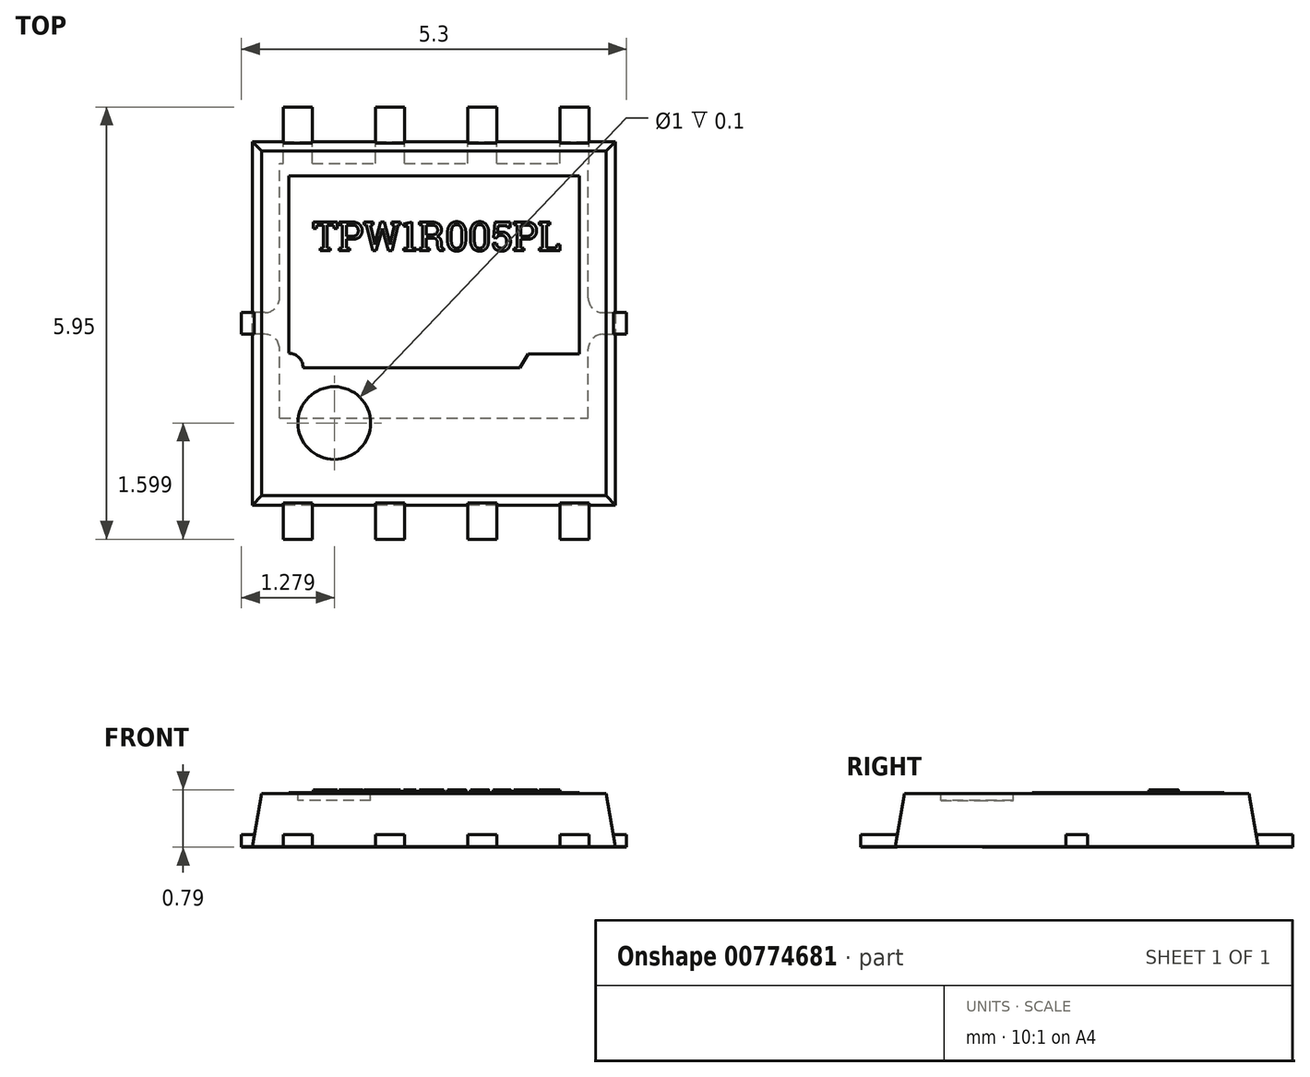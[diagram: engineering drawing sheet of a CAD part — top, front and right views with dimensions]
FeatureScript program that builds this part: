
annotation { "Feature Type Name" : "Feature", "Feature Type Description" : "" }
export const myFeature = defineFeature(function(context is Context, id is Id, definition is map)
    precondition{}
    {
        {
            var Q0;
            Q0=qCreatedBy(makeId("Top.planeOp"),FACE);
            cPlane(context, id + "F0", {"entities" : qUnion([Q0]), "cplaneType" : CPlaneType.OFFSET, "offset" : 0.17 * mm, "width" : 150 * mm, "height" : 150 * mm});
        }
        {
            var Q0;
            Q0=qCreatedBy(makeId("Top.planeOp"),FACE);
            var sketch = newSketch(context, id + "F1", { "sketchPlane" : qUnion([Q0])});
            skLineSegment(sketch, "E0.bottom", {"start": v(2.5, -2.5) * mm, "end": v(-2.5, -2.5) * mm});
            skLineSegment(sketch, "E0.top", {"start": v(2.5, 2.5) * mm, "end": v(-2.5, 2.5) * mm});
            skLineSegment(sketch, "E0.left", {"start": v(2.5, -2.5) * mm, "end": v(2.5, 2.5) * mm});
            skLineSegment(sketch, "E0.right", {"start": v(-2.5, -2.5) * mm, "end": v(-2.5, 2.5) * mm});
            skPoint(sketch, "E0.middle", {"position": v(0, 0) * mm});
            skSolve(sketch);
        }
        {
            var Q0;
            Q0 = qSketchRegion(id + "F1", true);
            extrude(context, id + "F2", {"entities" : qUnion([Q0]), "depth" : 0.73 * mm, "offsetDistance" : 25 * mm, "hasDraft" : true, "draftAngle" : 10 * degree, "draftPullDirection" : true});
        }
        {
            var Q0;
            Q0=qCreatedBy(id+"F0.planeOp",FACE);
            var sketch = newSketch(context, id + "F3", { "sketchPlane" : qUnion([Q0])});
            skLineSegment(sketch, "E1.bottom", {"start": v(-2.08, -2.47) * mm, "end": v(-1.68, -2.47) * mm});
            skLineSegment(sketch, "E1.top", {"start": v(-2.08, -2.97) * mm, "end": v(-1.68, -2.97) * mm});
            skLineSegment(sketch, "E1.left", {"start": v(-2.08, -2.47) * mm, "end": v(-2.08, -2.97) * mm});
            skLineSegment(sketch, "E1.right", {"start": v(-1.68, -2.47) * mm, "end": v(-1.68, -2.97) * mm});
            skLineSegment(sketch, "E2", {"start": v(-2.47, -2.47) * mm, "end": v(2.47, -2.47) * mm, "construction": true});
            skLineSegment(sketch, "E3", {"start": v(2.47, 2.47) * mm, "end": v(-2.47, 2.47) * mm, "construction": true});
            skLineSegment(sketch, "E4", {"start": v(2.47, -2.47) * mm, "end": v(2.47, 2.47) * mm, "construction": true});
            skLineSegment(sketch, "E5", {"start": v(-2.47, 2.47) * mm, "end": v(-2.47, -2.47) * mm, "construction": true});
            skSolve(sketch);
        }
        {
            var Q0;
            Q0=makeQuery(id+"F2.opExtrude","CAP_FACE",FACE,{"disambiguationData":[OSD([sQuery(id+"F1.wireOp",EDGE,"E0.bottom"),sQuery(id+"F1.wireOp",EDGE,"E0.top"),sQuery(id+"F1.wireOp",EDGE,"E0.left"),sQuery(id+"F1.wireOp",EDGE,"E0.right")])],"isStart":false});
            var sketch = newSketch(context, id + "F4", { "sketchPlane" : qUnion([Q0])});
            skCircle(sketch, "E6", {"center": v(-1.37, -1.37) * mm, "radius": 0.5 * mm});
            skSolve(sketch);
        }
        {
            var Q0;
            Q0=makeQuery(id+"F2.opExtrude","CAP_FACE",FACE,{"disambiguationData":[OSD([sQuery(id+"F1.wireOp",EDGE,"E0.bottom"),sQuery(id+"F1.wireOp",EDGE,"E0.top"),sQuery(id+"F1.wireOp",EDGE,"E0.left"),sQuery(id+"F1.wireOp",EDGE,"E0.right")])],"isStart":true});
            var sketch = newSketch(context, id + "F5", { "sketchPlane" : qUnion([Q0])});
            skLineSegment(sketch, "E7", {"start": v(0, 2.5) * mm, "end": v(0, -2.5) * mm, "construction": true});
            skLineSegment(sketch, "E8", {"start": v(-2.5, 0) * mm, "end": v(2.5, 0) * mm, "construction": true});
            skSolve(sketch);
        }
        {
            var Q0;
            Q0 = qSketchRegion(id + "F3", true);
            var Q1;
            Q1=makeQuery(id+"F2.opExtrude","CAP_FACE",FACE,{"disambiguationData":[OSD([sQuery(id+"F1.wireOp",EDGE,"E0.bottom"),sQuery(id+"F1.wireOp",EDGE,"E0.top"),sQuery(id+"F1.wireOp",EDGE,"E0.left"),sQuery(id+"F1.wireOp",EDGE,"E0.right")])],"isStart":true});
            extrude(context, id + "F6", {"entities" : qUnion([Q0]), "endBound" : BoundingType.UP_TO_SURFACE, "oppositeDirection" : true, "depth" : 25 * mm, "endBoundEntityFace" : qUnion([Q1]), "offsetDistance" : 25 * mm});
        }
        {
            var Q0;
            Q0=makeQuery(id+"F6.opExtrude","SWEPT_BODY",BODY,{"disambiguationData":[OSD([sQuery(id+"F3.wireOp",EDGE,"E1.bottom"),sQuery(id+"F3.wireOp",EDGE,"E1.top"),sQuery(id+"F3.wireOp",EDGE,"E1.left"),sQuery(id+"F3.wireOp",EDGE,"E1.right")])]});
            transform(context, id + "F7", {"entities" : qUnion([Q0]), "transformType" : TransformType.TRANSLATION_3D, "dx" : 1.27 * mm, "dy" : 0 * mm, "dz" : 0 * mm, "makeCopy" : true});
        }
        {
            var Q0;
            Q0=makeQuery(id+"F7.opPattern","COPY",BODY,{"derivedFrom":makeQuery(id+"F6.opExtrude","SWEPT_BODY",BODY,{"disambiguationData":[OSD([sQuery(id+"F3.wireOp",EDGE,"E1.bottom"),sQuery(id+"F3.wireOp",EDGE,"E1.top"),sQuery(id+"F3.wireOp",EDGE,"E1.left"),sQuery(id+"F3.wireOp",EDGE,"E1.right")])]}),"instanceName":"1"});
            transform(context, id + "F8", {"entities" : qUnion([Q0]), "transformType" : TransformType.TRANSLATION_3D, "dx" : 1.27 * mm, "dy" : 0 * mm, "dz" : 0 * mm, "makeCopy" : true});
        }
        {
            var Q0;
            Q0=makeQuery(id+"F8.opPattern","COPY",BODY,{"derivedFrom":makeQuery(id+"F7.opPattern","COPY",BODY,{"derivedFrom":makeQuery(id+"F6.opExtrude","SWEPT_BODY",BODY,{"disambiguationData":[OSD([sQuery(id+"F3.wireOp",EDGE,"E1.bottom"),sQuery(id+"F3.wireOp",EDGE,"E1.top"),sQuery(id+"F3.wireOp",EDGE,"E1.left"),sQuery(id+"F3.wireOp",EDGE,"E1.right")])]}),"instanceName":"1"}),"instanceName":"1"});
            transform(context, id + "F9", {"entities" : qUnion([Q0]), "transformType" : TransformType.TRANSLATION_3D, "dx" : 1.27 * mm, "dy" : 0 * mm, "dz" : 0 * mm, "makeCopy" : true});
        }
        {
            var Q0;
            Q0=makeQuery(id+"F6.opExtrude","SWEPT_BODY",BODY,{"disambiguationData":[OSD([sQuery(id+"F3.wireOp",EDGE,"E1.bottom"),sQuery(id+"F3.wireOp",EDGE,"E1.top"),sQuery(id+"F3.wireOp",EDGE,"E1.left"),sQuery(id+"F3.wireOp",EDGE,"E1.right")])]});
            transform(context, id + "F10", {"entities" : qUnion([Q0]), "transformType" : TransformType.TRANSLATION_3D, "dx" : 0 * mm, "dy" : 0 * mm, "dz" : 5.5 * mm, "makeCopy" : true});
        }
        {
            var Q0;
            Q0=makeQuery(id+"F10.opPattern","COPY",BODY,{"derivedFrom":makeQuery(id+"F6.opExtrude","SWEPT_BODY",BODY,{"disambiguationData":[OSD([sQuery(id+"F3.wireOp",EDGE,"E1.bottom"),sQuery(id+"F3.wireOp",EDGE,"E1.top"),sQuery(id+"F3.wireOp",EDGE,"E1.left"),sQuery(id+"F3.wireOp",EDGE,"E1.right")])]}),"instanceName":"1"});
            deleteBodies(context, id + "F11", {"entities" : qUnion([Q0])});
        }
        {
            var Q0;
            Q0=makeQuery(id+"F6.opExtrude","SWEPT_BODY",BODY,{"disambiguationData":[OSD([sQuery(id+"F3.wireOp",EDGE,"E1.bottom"),sQuery(id+"F3.wireOp",EDGE,"E1.top"),sQuery(id+"F3.wireOp",EDGE,"E1.left"),sQuery(id+"F3.wireOp",EDGE,"E1.right")])]});
            transform(context, id + "F12", {"entities" : qUnion([Q0]), "transformType" : TransformType.TRANSLATION_3D, "dx" : 0 * mm, "dy" : 5.4 * mm, "dz" : 0 * mm, "makeCopy" : true});
        }
        {
            var Q0;
            Q0=makeQuery(id+"F12.opPattern","COPY",BODY,{"derivedFrom":makeQuery(id+"F6.opExtrude","SWEPT_BODY",BODY,{"disambiguationData":[OSD([sQuery(id+"F3.wireOp",EDGE,"E1.bottom"),sQuery(id+"F3.wireOp",EDGE,"E1.top"),sQuery(id+"F3.wireOp",EDGE,"E1.left"),sQuery(id+"F3.wireOp",EDGE,"E1.right")])]}),"instanceName":"1"});
            transform(context, id + "F13", {"entities" : qUnion([Q0]), "transformType" : TransformType.TRANSLATION_3D, "dx" : 1.27 * mm, "dy" : 0 * mm, "dz" : 0 * mm, "makeCopy" : true});
        }
        {
            var Q0;
            Q0=makeQuery(id+"F13.opPattern","COPY",BODY,{"derivedFrom":makeQuery(id+"F12.opPattern","COPY",BODY,{"derivedFrom":makeQuery(id+"F6.opExtrude","SWEPT_BODY",BODY,{"disambiguationData":[OSD([sQuery(id+"F3.wireOp",EDGE,"E1.bottom"),sQuery(id+"F3.wireOp",EDGE,"E1.top"),sQuery(id+"F3.wireOp",EDGE,"E1.left"),sQuery(id+"F3.wireOp",EDGE,"E1.right")])]}),"instanceName":"1"}),"instanceName":"1"});
            transform(context, id + "F14", {"entities" : qUnion([Q0]), "transformType" : TransformType.TRANSLATION_3D, "dx" : 1.27 * mm, "dy" : 0 * mm, "dz" : 0 * mm, "makeCopy" : true});
        }
        {
            var Q0;
            Q0=makeQuery(id+"F14.opPattern","COPY",BODY,{"derivedFrom":makeQuery(id+"F13.opPattern","COPY",BODY,{"derivedFrom":makeQuery(id+"F12.opPattern","COPY",BODY,{"derivedFrom":makeQuery(id+"F6.opExtrude","SWEPT_BODY",BODY,{"disambiguationData":[OSD([sQuery(id+"F3.wireOp",EDGE,"E1.bottom"),sQuery(id+"F3.wireOp",EDGE,"E1.top"),sQuery(id+"F3.wireOp",EDGE,"E1.left"),sQuery(id+"F3.wireOp",EDGE,"E1.right")])]}),"instanceName":"1"}),"instanceName":"1"}),"instanceName":"1"});
            transform(context, id + "F15", {"entities" : qUnion([Q0]), "transformType" : TransformType.TRANSLATION_3D, "dx" : 1.27 * mm, "dy" : 0 * mm, "dz" : 0 * mm, "makeCopy" : true});
        }
        {
            var Q0;
            Q0 = qSketchRegion(id + "F4", true);
            extrude(context, id + "F16", {"entities" : qUnion([Q0]), "operationType" : NewBodyOperationType.REMOVE, "oppositeDirection" : true, "depth" : 0.1 * mm, "offsetDistance" : 25 * mm});
        }
        {
            var Q0;
            Q0=makeQuery(id+"F12.opPattern","COPY",BODY,{"derivedFrom":makeQuery(id+"F6.opExtrude","SWEPT_BODY",BODY,{"disambiguationData":[OSD([sQuery(id+"F3.wireOp",EDGE,"E1.bottom"),sQuery(id+"F3.wireOp",EDGE,"E1.top"),sQuery(id+"F3.wireOp",EDGE,"E1.left"),sQuery(id+"F3.wireOp",EDGE,"E1.right")])]}),"instanceName":"1"});
            transform(context, id + "F17", {"entities" : qUnion([Q0]), "transformType" : TransformType.TRANSLATION_3D, "dx" : 0 * mm, "dy" : 0.05 * mm, "dz" : 0 * mm, "makeCopy" : false});
        }
        {
            var Q0;
            Q0=makeQuery(id+"F13.opPattern","COPY",BODY,{"derivedFrom":makeQuery(id+"F12.opPattern","COPY",BODY,{"derivedFrom":makeQuery(id+"F6.opExtrude","SWEPT_BODY",BODY,{"disambiguationData":[OSD([sQuery(id+"F3.wireOp",EDGE,"E1.bottom"),sQuery(id+"F3.wireOp",EDGE,"E1.top"),sQuery(id+"F3.wireOp",EDGE,"E1.left"),sQuery(id+"F3.wireOp",EDGE,"E1.right")])]}),"instanceName":"1"}),"instanceName":"1"});
            transform(context, id + "F18", {"entities" : qUnion([Q0]), "transformType" : TransformType.TRANSLATION_3D, "dx" : 0 * mm, "dy" : 0.05 * mm, "dz" : 0 * mm, "makeCopy" : false});
        }
        {
            var Q0;
            Q0=makeQuery(id+"F14.opPattern","COPY",BODY,{"derivedFrom":makeQuery(id+"F13.opPattern","COPY",BODY,{"derivedFrom":makeQuery(id+"F12.opPattern","COPY",BODY,{"derivedFrom":makeQuery(id+"F6.opExtrude","SWEPT_BODY",BODY,{"disambiguationData":[OSD([sQuery(id+"F3.wireOp",EDGE,"E1.bottom"),sQuery(id+"F3.wireOp",EDGE,"E1.top"),sQuery(id+"F3.wireOp",EDGE,"E1.left"),sQuery(id+"F3.wireOp",EDGE,"E1.right")])]}),"instanceName":"1"}),"instanceName":"1"}),"instanceName":"1"});
            transform(context, id + "F19", {"entities" : qUnion([Q0]), "transformType" : TransformType.TRANSLATION_3D, "dx" : 0 * mm, "dy" : 0.05 * mm, "dz" : 0 * mm, "makeCopy" : false});
        }
        {
            var Q0;
            Q0=makeQuery(id+"F15.opPattern","COPY",BODY,{"derivedFrom":makeQuery(id+"F14.opPattern","COPY",BODY,{"derivedFrom":makeQuery(id+"F13.opPattern","COPY",BODY,{"derivedFrom":makeQuery(id+"F12.opPattern","COPY",BODY,{"derivedFrom":makeQuery(id+"F6.opExtrude","SWEPT_BODY",BODY,{"disambiguationData":[OSD([sQuery(id+"F3.wireOp",EDGE,"E1.bottom"),sQuery(id+"F3.wireOp",EDGE,"E1.top"),sQuery(id+"F3.wireOp",EDGE,"E1.left"),sQuery(id+"F3.wireOp",EDGE,"E1.right")])]}),"instanceName":"1"}),"instanceName":"1"}),"instanceName":"1"}),"instanceName":"1"});
            transform(context, id + "F20", {"entities" : qUnion([Q0]), "transformType" : TransformType.TRANSLATION_3D, "dx" : 0 * mm, "dy" : 0.05 * mm, "dz" : 0 * mm, "makeCopy" : true});
        }
        {
            var Q0;
            Q0=makeQuery(id+"F15.opPattern","COPY",BODY,{"derivedFrom":makeQuery(id+"F14.opPattern","COPY",BODY,{"derivedFrom":makeQuery(id+"F13.opPattern","COPY",BODY,{"derivedFrom":makeQuery(id+"F12.opPattern","COPY",BODY,{"derivedFrom":makeQuery(id+"F6.opExtrude","SWEPT_BODY",BODY,{"disambiguationData":[OSD([sQuery(id+"F3.wireOp",EDGE,"E1.bottom"),sQuery(id+"F3.wireOp",EDGE,"E1.top"),sQuery(id+"F3.wireOp",EDGE,"E1.left"),sQuery(id+"F3.wireOp",EDGE,"E1.right")])]}),"instanceName":"1"}),"instanceName":"1"}),"instanceName":"1"}),"instanceName":"1"});
            transform(context, id + "F21", {"entities" : qUnion([Q0]), "transformType" : TransformType.TRANSLATION_3D, "dx" : 0 * mm, "dy" : 0.05 * mm, "dz" : 0 * mm, "makeCopy" : false});
        }
        {
            var Q0;
            Q0=makeQuery(id+"F5.imprint","IMPRINT",FACE,{"disambiguationData":[TD([[makeQuery(id+"F5.imprint","IMPRINT",EDGE,{"derivedFrom":makeQuery(id+"F2.opExtrude","CAP_EDGE",EDGE,{"disambiguationData":[OSD([sQuery(id+"F1.wireOp",EDGE,"E0.bottom")])],"isStart":true})}),1.0]])]});
            var sketch = newSketch(context, id + "F22", { "sketchPlane" : qUnion([Q0])});
            skLineSegment(sketch, "E9.bottom", {"start": v(-2.12, 1.3) * mm, "end": v(2.12, 1.3) * mm});
            skLineSegment(sketch, "E9.top", {"start": v(-2.12, -2.2) * mm, "end": v(-2.08, -2.2) * mm});
            skLineSegment(sketch, "E9.left", {"start": v(-2.12, 1.3) * mm, "end": v(-2.12, 0.35) * mm});
            skLineSegment(sketch, "E9.right", {"start": v(2.12, 1.3) * mm, "end": v(2.12, 0.35) * mm});
            skLineSegment(sketch, "E10.top", {"start": v(-2.08, -2.98) * mm, "end": v(-1.68, -2.98) * mm});
            skLineSegment(sketch, "E10.left", {"start": v(-2.08, -2.2) * mm, "end": v(-2.08, -2.98) * mm});
            skLineSegment(sketch, "E10.right", {"start": v(-1.68, -2.2) * mm, "end": v(-1.68, -2.98) * mm});
            skLineSegment(sketch, "E11.top", {"start": v(-0.8, -2.98) * mm, "end": v(-0.4, -2.98) * mm});
            skLineSegment(sketch, "E11.left", {"start": v(-0.8, -2.2) * mm, "end": v(-0.8, -2.98) * mm});
            skLineSegment(sketch, "E11.right", {"start": v(-0.4, -2.2) * mm, "end": v(-0.4, -2.98) * mm});
            skLineSegment(sketch, "E12.top", {"start": v(0.46, -2.98) * mm, "end": v(0.86, -2.98) * mm});
            skLineSegment(sketch, "E12.left", {"start": v(0.46, -2.2) * mm, "end": v(0.46, -2.98) * mm});
            skLineSegment(sketch, "E12.right", {"start": v(0.86, -2.2) * mm, "end": v(0.86, -2.98) * mm});
            skLineSegment(sketch, "E13.bottom", {"start": v(2.12, -2.2) * mm, "end": v(2.13, -2.2) * mm});
            skLineSegment(sketch, "E13.top", {"start": v(1.73, -2.98) * mm, "end": v(2.13, -2.98) * mm});
            skLineSegment(sketch, "E13.left", {"start": v(1.73, -2.2) * mm, "end": v(1.73, -2.98) * mm});
            skLineSegment(sketch, "E13.right", {"start": v(2.13, -2.2) * mm, "end": v(2.13, -2.98) * mm});
            skLineSegment(sketch, "E14.trimOffspring", {"start": v(0.86, -2.2) * mm, "end": v(1.73, -2.2) * mm});
            skLineSegment(sketch, "E15.trimOffspring", {"start": v(-0.4, -2.2) * mm, "end": v(0.46, -2.2) * mm});
            skLineSegment(sketch, "E16.trimOffspring", {"start": v(-1.68, -2.2) * mm, "end": v(-0.8, -2.2) * mm});
            skLineSegment(sketch, "E17.bottom", {"start": v(-2.33, 0.15) * mm, "end": v(-2.65, 0.15) * mm});
            skLineSegment(sketch, "E17.top", {"start": v(-2.33, -0.15) * mm, "end": v(-2.65, -0.15) * mm});
            skLineSegment(sketch, "E17.right", {"start": v(-2.65, 0.15) * mm, "end": v(-2.65, -0.15) * mm});
            skLineSegment(sketch, "E18.bottom", {"start": v(2.33, 0.15) * mm, "end": v(2.65, 0.15) * mm});
            skLineSegment(sketch, "E18.top", {"start": v(2.33, -0.15) * mm, "end": v(2.65, -0.15) * mm});
            skLineSegment(sketch, "E18.right", {"start": v(2.65, 0.15) * mm, "end": v(2.65, -0.15) * mm});
            skLineSegment(sketch, "E19.trimOffspring", {"start": v(-2.12, -0.35) * mm, "end": v(-2.12, -2.2) * mm});
            skLineSegment(sketch, "E20.trimOffspring", {"start": v(2.12, -0.35) * mm, "end": v(2.12, -2.2) * mm});
            skPoint(sketch, "E21.visualSharp", {"position": v(-2.12, 0.15) * mm});
            skArc(sketch, "E21.filletArc", {"start": v(-2.33, 0.15) * mm, "mid": v(-2.18, 0.2) * mm, "end": v(-2.12, 0.35) * mm});
            skPoint(sketch, "E22.visualSharp", {"position": v(-2.12, -0.15) * mm});
            skArc(sketch, "E22.filletArc", {"start": v(-2.12, -0.35) * mm, "mid": v(-2.18, -0.2) * mm, "end": v(-2.33, -0.15) * mm});
            skPoint(sketch, "E23.visualSharp", {"position": v(2.12, 0.15) * mm});
            skArc(sketch, "E23.filletArc", {"start": v(2.12, 0.35) * mm, "mid": v(2.18, 0.2) * mm, "end": v(2.33, 0.15) * mm});
            skPoint(sketch, "E24.visualSharp", {"position": v(2.12, -0.15) * mm});
            skArc(sketch, "E24.filletArc", {"start": v(2.33, -0.15) * mm, "mid": v(2.18, -0.2) * mm, "end": v(2.12, -0.35) * mm});
            skLineSegment(sketch, "E25.bottom", {"start": v(-2.08, 2.97) * mm, "end": v(-1.68, 2.97) * mm});
            skLineSegment(sketch, "E25.top", {"start": v(-2.08, 2.47) * mm, "end": v(-1.68, 2.47) * mm});
            skLineSegment(sketch, "E25.left", {"start": v(-2.08, 2.97) * mm, "end": v(-2.08, 2.47) * mm});
            skLineSegment(sketch, "E25.right", {"start": v(-1.68, 2.97) * mm, "end": v(-1.68, 2.47) * mm});
            skLineSegment(sketch, "E26.bottom", {"start": v(-0.8, 2.97) * mm, "end": v(-0.4, 2.97) * mm});
            skLineSegment(sketch, "E26.top", {"start": v(-0.8, 2.47) * mm, "end": v(-0.4, 2.47) * mm});
            skLineSegment(sketch, "E26.left", {"start": v(-0.8, 2.97) * mm, "end": v(-0.8, 2.47) * mm});
            skLineSegment(sketch, "E26.right", {"start": v(-0.4, 2.97) * mm, "end": v(-0.4, 2.47) * mm});
            skLineSegment(sketch, "E27.bottom", {"start": v(0.46, 2.97) * mm, "end": v(0.86, 2.97) * mm});
            skLineSegment(sketch, "E27.top", {"start": v(0.46, 2.47) * mm, "end": v(0.86, 2.47) * mm});
            skLineSegment(sketch, "E27.left", {"start": v(0.46, 2.97) * mm, "end": v(0.46, 2.47) * mm});
            skLineSegment(sketch, "E27.right", {"start": v(0.86, 2.97) * mm, "end": v(0.86, 2.47) * mm});
            skLineSegment(sketch, "E28.bottom", {"start": v(1.73, 2.97) * mm, "end": v(2.13, 2.97) * mm});
            skLineSegment(sketch, "E28.top", {"start": v(1.73, 2.47) * mm, "end": v(2.13, 2.47) * mm});
            skLineSegment(sketch, "E28.left", {"start": v(1.73, 2.97) * mm, "end": v(1.73, 2.47) * mm});
            skLineSegment(sketch, "E28.right", {"start": v(2.13, 2.97) * mm, "end": v(2.13, 2.47) * mm});
            skSolve(sketch);
        }
        {
            var Q0;
            Q0 = qSketchRegion(id + "F22", true);
            extrude(context, id + "F23", {"entities" : qUnion([Q0]), "depth" : 0.01 * mm, "offsetDistance" : 25 * mm});
        }
        {
            var Q0;
            Q0=makeQuery(id+"F2.opExtrude","CAP_FACE",FACE,{"disambiguationData":[OSD([sQuery(id+"F1.wireOp",EDGE,"E0.bottom"),sQuery(id+"F1.wireOp",EDGE,"E0.top"),sQuery(id+"F1.wireOp",EDGE,"E0.left"),sQuery(id+"F1.wireOp",EDGE,"E0.right")])],"isStart":false});
            var sketch = newSketch(context, id + "F24", { "sketchPlane" : qUnion([Q0])});
            skText(sketch, "E29", { "text": "TPW1R005PL", "fontName": "RobotoSlab-Regular.ttf"});
            const initialGuessF24  = {"E29": [-0.00167, 0.001, 1, 0, 0.0004]};
            skSetInitialGuess(sketch, initialGuessF24);
            skSolve(sketch);
        }
        {
            var Q0;
            Q0 = qSketchRegion(id + "F24", true);
            extrude(context, id + "F25", {"entities" : qUnion([Q0]), "operationType" : NewBodyOperationType.ADD, "depth" : 0.05 * mm, "offsetDistance" : 25 * mm});
        }
        {
            var Q0;
            Q0=qCreatedBy(id+"F0.planeOp",FACE);
            var sketch = newSketch(context, id + "F26", { "sketchPlane" : qUnion([Q0])});
            skLineSegment(sketch, "E30.bottom", {"start": v(2.47, -0.15) * mm, "end": v(2.65, -0.15) * mm});
            skLineSegment(sketch, "E30.top", {"start": v(2.47, 0.15) * mm, "end": v(2.65, 0.15) * mm});
            skLineSegment(sketch, "E30.left", {"start": v(2.47, -0.15) * mm, "end": v(2.47, 0.15) * mm});
            skLineSegment(sketch, "E30.right", {"start": v(2.65, -0.15) * mm, "end": v(2.65, 0.15) * mm});
            skLineSegment(sketch, "E31.bottom", {"start": v(-2.65, 0.15) * mm, "end": v(-2.47, 0.15) * mm});
            skLineSegment(sketch, "E31.top", {"start": v(-2.65, -0.15) * mm, "end": v(-2.47, -0.15) * mm});
            skLineSegment(sketch, "E31.left", {"start": v(-2.65, 0.15) * mm, "end": v(-2.65, -0.15) * mm});
            skLineSegment(sketch, "E31.right", {"start": v(-2.47, 0.15) * mm, "end": v(-2.47, -0.15) * mm});
            skSolve(sketch);
        }
        {
            var Q0;
            Q0 = qSketchRegion(id + "F26", true);
            var Q1;
            Q1=makeQuery(id+"F23.opExtrude","CAP_FACE",FACE,{"disambiguationData":[OSD([sQuery(id+"F22.wireOp",EDGE,"E9.bottom"),sQuery(id+"F22.wireOp",EDGE,"E9.top"),sQuery(id+"F22.wireOp",EDGE,"E9.left"),sQuery(id+"F22.wireOp",EDGE,"E9.right"),sQuery(id+"F22.wireOp",EDGE,"E10.top"),sQuery(id+"F22.wireOp",EDGE,"E10.left"),sQuery(id+"F22.wireOp",EDGE,"E10.right"),sQuery(id+"F22.wireOp",EDGE,"E11.top"),sQuery(id+"F22.wireOp",EDGE,"E11.left"),sQuery(id+"F22.wireOp",EDGE,"E11.right"),sQuery(id+"F22.wireOp",EDGE,"E12.top"),sQuery(id+"F22.wireOp",EDGE,"E12.left"),sQuery(id+"F22.wireOp",EDGE,"E12.right"),sQuery(id+"F22.wireOp",EDGE,"E13.bottom"),sQuery(id+"F22.wireOp",EDGE,"E13.top"),sQuery(id+"F22.wireOp",EDGE,"E13.left"),sQuery(id+"F22.wireOp",EDGE,"E13.right"),sQuery(id+"F22.wireOp",EDGE,"E14.trimOffspring"),sQuery(id+"F22.wireOp",EDGE,"E15.trimOffspring"),sQuery(id+"F22.wireOp",EDGE,"E16.trimOffspring"),sQuery(id+"F22.wireOp",EDGE,"E17.bottom"),sQuery(id+"F22.wireOp",EDGE,"E17.top"),sQuery(id+"F22.wireOp",EDGE,"E17.right"),sQuery(id+"F22.wireOp",EDGE,"E18.bottom"),sQuery(id+"F22.wireOp",EDGE,"E18.top"),sQuery(id+"F22.wireOp",EDGE,"E18.right"),sQuery(id+"F22.wireOp",EDGE,"E19.trimOffspring"),sQuery(id+"F22.wireOp",EDGE,"E20.trimOffspring"),sQuery(id+"F22.wireOp",EDGE,"E21.filletArc"),sQuery(id+"F22.wireOp",EDGE,"E22.filletArc"),sQuery(id+"F22.wireOp",EDGE,"E23.filletArc"),sQuery(id+"F22.wireOp",EDGE,"E24.filletArc")])],"isStart":true});
            extrude(context, id + "F27", {"entities" : qUnion([Q0]), "endBound" : BoundingType.UP_TO_SURFACE, "oppositeDirection" : true, "depth" : 25 * mm, "endBoundEntityFace" : qUnion([Q1]), "offsetDistance" : 25 * mm});
        }
        {
            var Q0;
            Q0=makeQuery(id+"F20.opPattern","COPY",BODY,{"derivedFrom":makeQuery(id+"F15.opPattern","COPY",BODY,{"derivedFrom":makeQuery(id+"F14.opPattern","COPY",BODY,{"derivedFrom":makeQuery(id+"F13.opPattern","COPY",BODY,{"derivedFrom":makeQuery(id+"F12.opPattern","COPY",BODY,{"derivedFrom":makeQuery(id+"F6.opExtrude","SWEPT_BODY",BODY,{"disambiguationData":[OSD([sQuery(id+"F3.wireOp",EDGE,"E1.bottom"),sQuery(id+"F3.wireOp",EDGE,"E1.top"),sQuery(id+"F3.wireOp",EDGE,"E1.left"),sQuery(id+"F3.wireOp",EDGE,"E1.right")])]}),"instanceName":"1"}),"instanceName":"1"}),"instanceName":"1"}),"instanceName":"1"}),"instanceName":"1"});
            deleteBodies(context, id + "F28", {"entities" : qUnion([Q0])});
        }
        {
            var Q0;
            Q0=makeQuery(id+"F4.imprint","IMPRINT",FACE,{"disambiguationData":[TD([[makeQuery(id+"F4.imprint","IMPRINT",EDGE,{"derivedFrom":sQuery(id+"F4.wireOp",EDGE,"E6")}),-1.0]])]});
            var sketch = newSketch(context, id + "F29", { "sketchPlane" : qUnion([Q0])});
            skLineSegment(sketch, "E32", {"start": v(-2.37, 0) * mm, "end": v(2.37, 0) * mm, "construction": true});
            skLineSegment(sketch, "E33", {"start": v(0, 2.37) * mm, "end": v(0, -2.37) * mm, "construction": true});
            skLineSegment(sketch, "E34", {"start": v(-2, 2.03) * mm, "end": v(2, 2.03) * mm});
            skLineSegment(sketch, "E35", {"start": v(2, 2.03) * mm, "end": v(2, -0.42) * mm});
            skLineSegment(sketch, "E36", {"start": v(2, -0.42) * mm, "end": v(1.3, -0.42) * mm});
            skLineSegment(sketch, "E37", {"start": v(1.3, -0.42) * mm, "end": v(1.2, -0.6) * mm});
            skLineSegment(sketch, "E38", {"start": v(1.2, -0.6) * mm, "end": v(-1.8, -0.61) * mm});
            skLineSegment(sketch, "E39", {"start": v(-2, -0.41) * mm, "end": v(-2, 2.03) * mm});
            skArc(sketch, "E40", {"start": v(-1.8, -0.61) * mm, "mid": v(-1.86, -0.47) * mm, "end": v(-2, -0.41) * mm});
            skSolve(sketch);
        }
        {
            var Q0;
            Q0=makeQuery(id+"F29.imprint","IMPRINT",FACE,{"disambiguationData":[TD([[makeQuery(id+"F29.imprint","IMPRINT",EDGE,{"derivedFrom":sQuery(id+"F29.wireOp",EDGE,"E34")}),1.0]])]});
            var sketch = newSketch(context, id + "F30", { "sketchPlane" : qUnion([Q0])});
            skLineSegment(sketch, "E41", {"start": v(-2, 2.03) * mm, "end": v(2, 2.03) * mm});
            skLineSegment(sketch, "E42", {"start": v(2, 2.03) * mm, "end": v(2, -0.42) * mm});
            skLineSegment(sketch, "E43", {"start": v(2, -0.42) * mm, "end": v(1.3, -0.42) * mm});
            skLineSegment(sketch, "E44", {"start": v(1.3, -0.42) * mm, "end": v(1.18, -0.61) * mm});
            skLineSegment(sketch, "E45", {"start": v(1.18, -0.61) * mm, "end": v(-1.8, -0.61) * mm});
            skLineSegment(sketch, "E46", {"start": v(-2, -0.41) * mm, "end": v(-2, 2.03) * mm});
            skArc(sketch, "E47", {"start": v(-1.8, -0.61) * mm, "mid": v(-1.86, -0.47) * mm, "end": v(-2, -0.41) * mm});
            skSolve(sketch);
        }
        {
            var Q0;
            Q0 = qSketchRegion(id + "F30", true);
            extrude(context, id + "F31", {"entities" : qUnion([Q0]), "depth" : 0.01 * mm, "offsetDistance" : 25 * mm});
        }
    });
